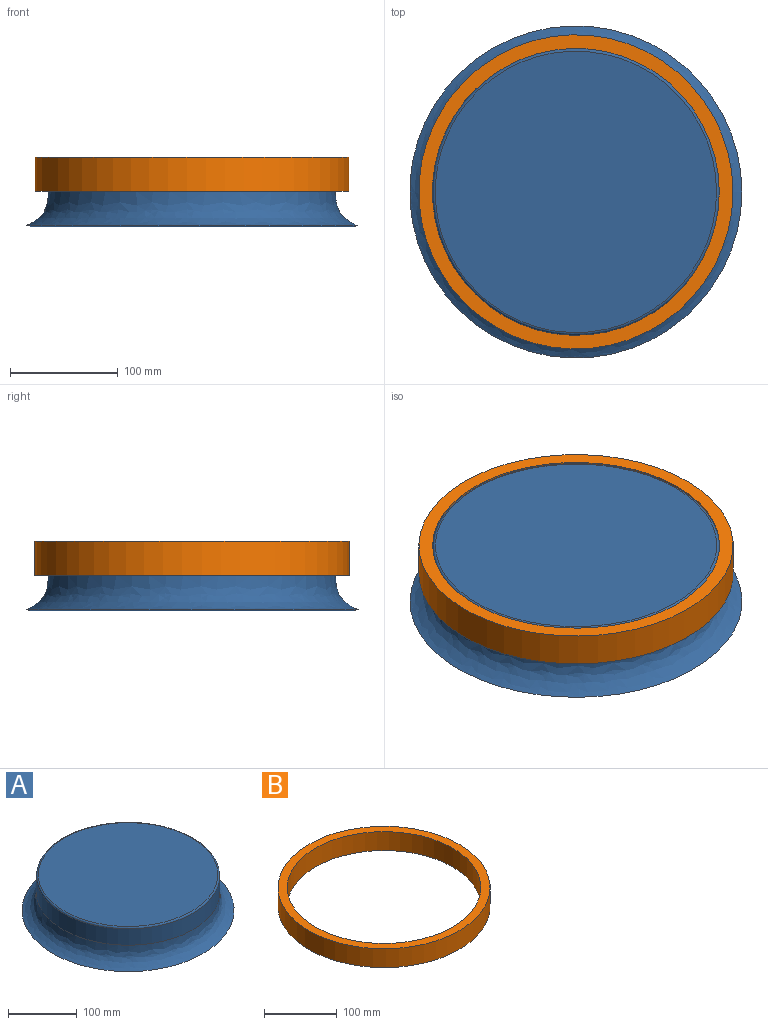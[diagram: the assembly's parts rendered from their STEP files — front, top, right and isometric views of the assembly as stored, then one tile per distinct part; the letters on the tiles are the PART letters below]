
ASSEMBLY  parts=2 mates=1
PART A: 8 faces, bbox 308.8x308.8x64.9 mm
  f0: cylinder r=133.35mm len=266.7mm, axis (0,0,-1), area 24474mm2, adj f2,f7
  f1: plane 261.62x261.62mm, normal (0,0,1), area 53756.6mm2, adj f7
  f2: revolved ~308.77x308.77mm, area 36626mm2, adj f0,f3
  f3: cone r=154.38mm half-angle=80.8deg, axis (0,0,1), area 6100mm2, adj f2,f4
  f4: revolved ~296.09x296.09mm, area 35718.2mm2, adj f3,f5
  f5: cylinder r=127mm len=254mm, axis (0,0,1), area 20268.3mm2, adj f4,f6
  f6: plane 254x254mm, normal (0,0,-1), area 50670.7mm2, adj f5
  f7: torus R=130.81mm, axis (0,0,1), area 3319.8mm2, adj f0,f1
PART B: 4 faces, bbox 292.1x292.1x31.8 mm
  f0: cylinder r=133.35mm len=266.7mm, axis (0,0,-1), area 26602.1mm2, adj f2,f3
  f1: cylinder r=146.05mm len=292.1mm, axis (0,0,-1), area 29135.7mm2, adj f2,f3
  f2: plane 292.1x292.1mm, normal (0,0,1), area 11147.6mm2, adj f0,f1
  f3: plane 292.1x292.1mm, normal (0,0,-1), area 11147.6mm2, adj f0,f1
PLACE A at identity fixed
PLACE B t=(0,0,-136.4)mm
MATE slider B.f0 <-> A.f0  axis (0,0,1) through (0,0,6.35)mm
